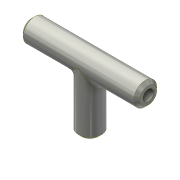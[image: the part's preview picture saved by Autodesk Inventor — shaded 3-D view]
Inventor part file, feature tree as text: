
AUTODESK INVENTOR PART (.ipt)
format: ipt  version: 2021 (Build 250183000, 183)  size: 156,672 bytes
history: native  units: mm
features: sketch x4, revolve x2, extrude x2, projected_geometry x2, other x1, fillet x1
ambient origin geometry x8: Origin, YZ Plane, XZ Plane, XY Plane, X Axis, Y Axis, Z Axis, Center Point
bodies: Body1 (feature_tree)
feature tree (12):
  other  "Твердое тело1"
  revolve  "Вращение1"
  revolve  "Вращение2"
  extrude  "Выдавливание1"  Depth=3.75mm
  extrude  "Выдавливание2"  Depth=2.0mm
  fillet  "Сопряжение1"  Radius=1.0mm
  sketch  "Эскиз1"
  sketch  "Эскиз3"
  sketch  "Эскиз4"
  projected_geometry  "Спроецированная петля1"
  sketch  "Эскиз5"
  projected_geometry  "Спроецированная петля2"
